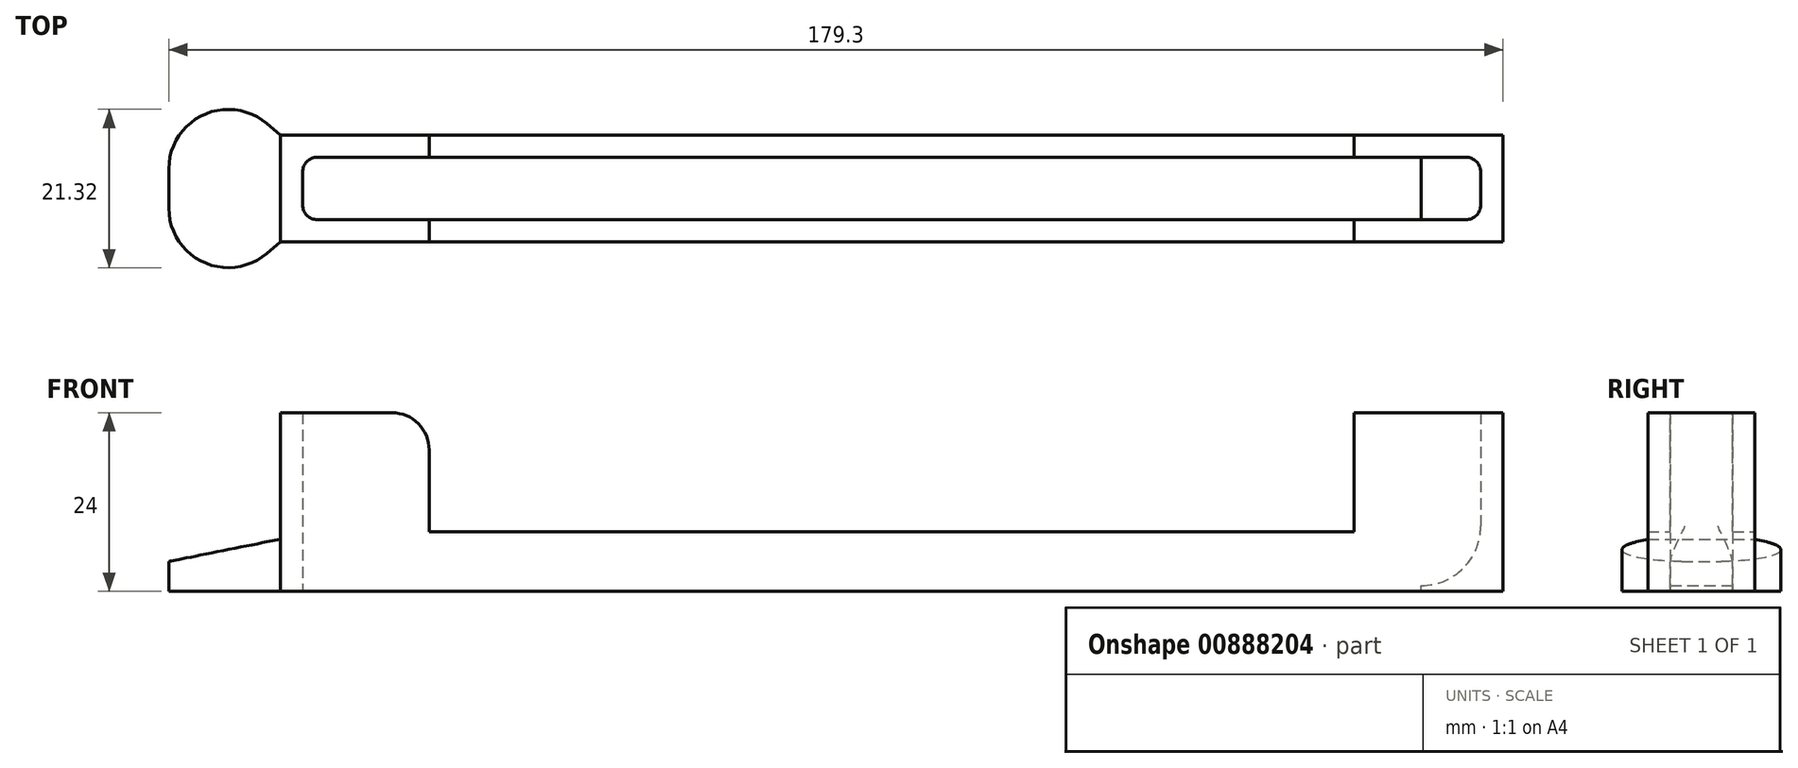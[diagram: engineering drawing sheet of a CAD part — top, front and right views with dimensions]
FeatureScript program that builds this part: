
annotation { "Feature Type Name" : "Feature", "Feature Type Description" : "" }
export const myFeature = defineFeature(function(context is Context, id is Id, definition is map)
    precondition{}
    {
        {
            assignVariable(context, id + "F0", {"name" : "gap", "anyValue" : .1});
        }
        {
            var Q0;
            Q0=qCreatedBy(makeId("Top.planeOp"),FACE);
            var sketch = newSketch(context, id + "F1", { "sketchPlane" : qUnion([Q0])});
            skLineSegment(sketch, "E0.bottom", {"start": v(79.15, -4.2) * mm, "end": v(-79.15, -4.2) * mm});
            skLineSegment(sketch, "E0.top", {"start": v(79.15, 4.2) * mm, "end": v(-79.15, 4.2) * mm});
            skLineSegment(sketch, "E0.left", {"start": v(79.15, -4.2) * mm, "end": v(79.15, 4.2) * mm});
            skLineSegment(sketch, "E0.right", {"start": v(-79.15, -4.2) * mm, "end": v(-79.15, 4.2) * mm});
            skPoint(sketch, "E0.middle", {"position": v(0, 0) * mm});
            skLineSegment(sketch, "E1.bottom", {"start": v(82.15, -7.2) * mm, "end": v(-82.15, -7.2) * mm});
            skLineSegment(sketch, "E1.top", {"start": v(82.15, 7.2) * mm, "end": v(-82.15, 7.2) * mm});
            skLineSegment(sketch, "E1.left", {"start": v(82.15, -7.2) * mm, "end": v(82.15, 7.2) * mm});
            skLineSegment(sketch, "E1.right", {"start": v(-82.15, -7.2) * mm, "end": v(-82.15, 7.2) * mm});
            skSolve(sketch);
        }
        {
            var Q0;
            Q0 = qSketchRegion(id + "F1", true);
            extrude(context, id + "F2", {"entities" : qUnion([Q0]), "depth" : 24 * mm, "offsetDistance" : 25 * mm});
        }
        {
            var Q0;
            Q0=makeQuery(id+"F2.opExtrude","SWEPT_EDGE",EDGE,{"disambiguationData":[OSD([sQuery(id+"F1.wireOp",EDGE,"E0.bottom"),sQuery(id+"F1.wireOp",EDGE,"E0.left")])]});
            var Q1;
            Q1=makeQuery(id+"F2.opExtrude","SWEPT_EDGE",EDGE,{"disambiguationData":[OSD([sQuery(id+"F1.wireOp",EDGE,"E0.top"),sQuery(id+"F1.wireOp",EDGE,"E0.left")])]});
            var Q2;
            Q2=makeQuery(id+"F2.opExtrude","SWEPT_EDGE",EDGE,{"disambiguationData":[OSD([sQuery(id+"F1.wireOp",EDGE,"E0.bottom"),sQuery(id+"F1.wireOp",EDGE,"E0.right")])]});
            var Q3;
            Q3=makeQuery(id+"F2.opExtrude","SWEPT_EDGE",EDGE,{"disambiguationData":[OSD([sQuery(id+"F1.wireOp",EDGE,"E0.top"),sQuery(id+"F1.wireOp",EDGE,"E0.right")])]});
            fillet(context, id + "F3", {"entities" : qUnion([Q0, Q1, Q2, Q3]), "radius" : 2 * mm, "tangentPropagation" : true, "allowEdgeOverflow" : false});
        }
        {
            var Q0;
            Q0=qCreatedBy(makeId("Front.planeOp"),FACE);
            var sketch = newSketch(context, id + "F4", { "sketchPlane" : qUnion([Q0])});
            skArc(sketch, "E2", {"start": v(71.15, 0.75) * mm, "mid": v(76.8, 3.1) * mm, "end": v(79.15, 8.75) * mm});
            skLineSegment(sketch, "E3", {"start": v(79.15, 8.75) * mm, "end": v(82.15, 8.75) * mm});
            skLineSegment(sketch, "E4", {"start": v(82.15, 8.75) * mm, "end": v(82.15, 0) * mm});
            skLineSegment(sketch, "E5", {"start": v(71.15, 0.75) * mm, "end": v(71.15, 0) * mm});
            skLineSegment(sketch, "E6", {"start": v(71.15, 0) * mm, "end": v(82.15, 0) * mm});
            skSolve(sketch);
        }
        {
            var Q0;
            Q0 = qSketchRegion(id + "F4", true);
            extrude(context, id + "F5", {"entities" : qUnion([Q0]), "operationType" : NewBodyOperationType.ADD, "endBound" : BoundingType.SYMMETRIC, "depth" : (8.5 + (2 * getVariable(context, 'gap'))) * mm, "offsetDistance" : 25 * mm});
        }
        {
            var Q0;
            Q0=makeQuery(id+"F2.opExtrude","SWEPT_FACE",FACE,{"disambiguationData":[OSD([sQuery(id+"F1.wireOp",EDGE,"E1.right")])]});
            var sketch = newSketch(context, id + "F6", { "sketchPlane" : qUnion([Q0])});
            skLineSegment(sketch, "E7.bottom", {"start": v(7.2, 0) * mm, "end": v(-7.2, 0) * mm});
            skLineSegment(sketch, "E7.top", {"start": v(7.2, 7) * mm, "end": v(-7.2, 7) * mm});
            skLineSegment(sketch, "E7.left", {"start": v(7.2, 0) * mm, "end": v(7.2, 7) * mm});
            skLineSegment(sketch, "E7.right", {"start": v(-7.2, 0) * mm, "end": v(-7.2, 7) * mm});
            skPoint(sketch, "E8", {"position": v(7.2, 12) * mm});
            skSolve(sketch);
        }
        {
            var Q0;
            Q0=makeQuery(id+"F6.imprint","IMPRINT",FACE,{"disambiguationData":[TD([[makeQuery(id+"F6.imprint","IMPRINT",EDGE,{"derivedFrom":sQuery(id+"F6.wireOp",EDGE,"E7.bottom")}),-1.0]])]});
            cPlane(context, id + "F7", {"entities" : qUnion([Q0]), "cplaneType" : CPlaneType.OFFSET, "offset" : 15 * mm, "width" : 150 * mm, "height" : 150 * mm});
        }
        {
            var Q0;
            Q0=qCreatedBy(id+"F7.planeOp",FACE);
            var sketch = newSketch(context, id + "F8", { "sketchPlane" : qUnion([Q0])});
            skLineSegment(sketch, "E9.bottom", {"start": v(20, 0) * mm, "end": v(-20, 0) * mm});
            skLineSegment(sketch, "E9.top", {"start": v(20, 4) * mm, "end": v(-20, 4) * mm});
            skLineSegment(sketch, "E9.left", {"start": v(20, 0) * mm, "end": v(20, 4) * mm});
            skLineSegment(sketch, "E9.right", {"start": v(-20, 0) * mm, "end": v(-20, 4) * mm});
            skSolve(sketch);
        }
        {
            var Q1;
            Q1 = qSketchRegion(id + "F6", true);
            var Q2;
            Q2 = qSketchRegion(id + "F8", true);
            loft(context, id + "F9", {"operationType" : NewBodyOperationType.ADD, "sheetProfilesArray" : [{ "sheetProfileEntities" : qUnion([Q1]) }, { "sheetProfileEntities" : qUnion([Q2]) }]});
        }
        {
            var Q0;
            Q0=makeQuery(id+"Frt0GUivWiWnZhL_1.1.F9.opLoft","MID_CAP_EDGE",EDGE,{"disambiguationData":[OSD([sQuery(id+"F8.wireOp",EDGE,"E9.bottom"),sQuery(id+"F8.wireOp",EDGE,"E9.top"),sQuery(id+"F8.wireOp",EDGE,"E9.left")])],"capPos":1.0});
            var Q1;
            Q1=makeQuery(id+"Frt0GUivWiWnZhL_1.1.F9.opLoft","MID_CAP_EDGE",EDGE,{"disambiguationData":[OSD([sQuery(id+"F8.wireOp",EDGE,"E9.bottom"),sQuery(id+"F8.wireOp",EDGE,"E9.top"),sQuery(id+"F8.wireOp",EDGE,"E9.right")])],"capPos":1.0});
            var Q2;
            Q2=makeQuery(id+"F9.opLoft","MID_CAP_EDGE",EDGE,{"disambiguationData":[OSD([sQuery(id+"F8.wireOp",EDGE,"E9.bottom"),sQuery(id+"F8.wireOp",EDGE,"E9.top"),sQuery(id+"F8.wireOp",EDGE,"E9.right")])],"capPos":1.0});
            var Q3;
            Q3=makeQuery(id+"F9.opLoft","MID_CAP_EDGE",EDGE,{"disambiguationData":[OSD([sQuery(id+"F8.wireOp",EDGE,"E9.bottom"),sQuery(id+"F8.wireOp",EDGE,"E9.top"),sQuery(id+"F8.wireOp",EDGE,"E9.left")])],"capPos":1.0});
            fillet(context, id + "F10", {"entities" : qUnion([Q0, Q1, Q2, Q3]), "radius" : 8 * mm, "tangentPropagation" : true, "allowEdgeOverflow" : false});
        }
        {
            var Q0;
            Q0=makeQuery(id+"F2.opExtrude","CAP_FACE",FACE,{"disambiguationData":[OSD([sQuery(id+"F1.wireOp",EDGE,"E0.bottom"),sQuery(id+"F1.wireOp",EDGE,"E0.top"),sQuery(id+"F1.wireOp",EDGE,"E0.left"),sQuery(id+"F1.wireOp",EDGE,"E0.right"),sQuery(id+"F1.wireOp",EDGE,"E1.bottom"),sQuery(id+"F1.wireOp",EDGE,"E1.top"),sQuery(id+"F1.wireOp",EDGE,"E1.left"),sQuery(id+"F1.wireOp",EDGE,"E1.right")])],"isStart":false});
            var sketch = newSketch(context, id + "F11", { "sketchPlane" : qUnion([Q0])});
            skLineSegment(sketch, "E10.bottom", {"start": v(-62.15, -7.2) * mm, "end": v(62.15, -7.2) * mm});
            skLineSegment(sketch, "E10.top", {"start": v(-62.15, 7.2) * mm, "end": v(62.15, 7.2) * mm});
            skLineSegment(sketch, "E10.left", {"start": v(-62.15, -7.2) * mm, "end": v(-62.15, 7.2) * mm});
            skLineSegment(sketch, "E10.right", {"start": v(62.15, -7.2) * mm, "end": v(62.15, 7.2) * mm});
            skSolve(sketch);
        }
        {
            var Q0;
            Q0 = qSketchRegion(id + "F11", true);
            extrude(context, id + "F12", {"entities" : qUnion([Q0]), "operationType" : NewBodyOperationType.REMOVE, "oppositeDirection" : true, "depth" : 16 * mm, "offsetDistance" : 25 * mm});
        }
        {
            var Q0;
            {var subQ1=sQuery(id+"F1.wireOp",EDGE,"E0.top");var subQ2=sQuery(id+"F11.wireOp",EDGE,"E10.left");Q0=makeQuery(id+"F12.boolean.opBoolean","COPY",EDGE,{"disambiguationData":[TD([makeQuery(id+"F2.opExtrude","SWEPT_FACE",FACE,{"disambiguationData":[OSD([subQ1])]})])],"derivedFrom":makeQuery(id+"F12.opExtrude","CAP_EDGE",EDGE,{"disambiguationData":[OSD([subQ2])],"isStart":true})});}
            var Q1;
            {var subQ0=sQuery(id+"F1.wireOp",EDGE,"E0.bottom");var subQ1=sQuery(id+"F11.wireOp",EDGE,"E10.left");Q1=makeQuery(id+"F12.boolean.opBoolean","COPY",EDGE,{"disambiguationData":[TD([makeQuery(id+"F2.opExtrude","SWEPT_FACE",FACE,{"disambiguationData":[OSD([subQ0])]})])],"derivedFrom":makeQuery(id+"F12.opExtrude","CAP_EDGE",EDGE,{"disambiguationData":[OSD([subQ1])],"isStart":true})});}
            var Q2;
            {var subQ1=sQuery(id+"F1.wireOp",EDGE,"E0.top");var subQ2=sQuery(id+"F11.wireOp",EDGE,"E10.right");Q2=makeQuery(id+"F12.boolean.opBoolean","COPY",EDGE,{"disambiguationData":[TD([makeQuery(id+"F2.opExtrude","SWEPT_FACE",FACE,{"disambiguationData":[OSD([subQ1])]})])],"derivedFrom":makeQuery(id+"F12.opExtrude","CAP_EDGE",EDGE,{"disambiguationData":[OSD([subQ2])],"isStart":true})});}
            var Q3;
            {var subQ0=sQuery(id+"F1.wireOp",EDGE,"E0.bottom");var subQ2=sQuery(id+"F11.wireOp",EDGE,"E10.right");Q3=makeQuery(id+"F12.boolean.opBoolean","COPY",EDGE,{"disambiguationData":[TD([makeQuery(id+"F2.opExtrude","SWEPT_FACE",FACE,{"disambiguationData":[OSD([subQ0])]})])],"derivedFrom":makeQuery(id+"F12.opExtrude","CAP_EDGE",EDGE,{"disambiguationData":[OSD([subQ2])],"isStart":true})});}
            fillet(context, id + "F13", {"entities" : qUnion([Q0, Q1, Q2, Q3]), "radius" : 5 * mm, "tangentPropagation" : true, "allowEdgeOverflow" : false});
        }
    });
